# Revit family: FTXL Boiler.rfa
name_source: partatom
category: Mechanical Equipment
revit_build: Autodesk Revit MEP 2012 (Build: 20110916_2132(x64)
units: mm (PartAtom-declared; Revit-internal decimal feet)

## types (5) — shared parameters
# of Electrical Connections = 1
AIR INLET SIZE = 4"
Air Inlet Radius = 2"
Back Clearance = 24"
DEPTH = 22 1/2"
Description = FTXL Fire Tube Boiler
FUEL TYPE = NATURAL GAS
Front Clearance = 30"
Fuel Type = Natural or LP
GAS SIZE = 1"
Gas Radius = 1/2"
HEIGHT = 53 1/2"
Manufacturer = Lochinvar
Offset to Gas = 23 1/4"
SES BIM Studio # = 201464901-1
Top Clearance = 24"
URL = http://www.lochinvar.com
Voltage/Control = 24
Voltage/Heater = 120
WIDTH = 26 1/4"

## per-type parameters (varying)
| type | A_Total Depth | B_Depth to Flue Centerline | C_Flue Offset | D_Water Inlet Offset | E_Air Inlet Offset | F_Air Inlet Height | G_Gas Conn Height | H_Water Inlet Height | INPUT RATE (BTUH) | VENT SIZE | Vent Radius | WATER INLET SIZE | WATER OUTLET SIZE | Water Inlet Radius | Water Outlet Radius |
| FTX400 | 30 1/2" | 27 1/2" | 10 1/4" | 17" | 23 1/4" | 46 1/4" | 39 1/2" | 10 3/4" | 399.9 | 4" | 2" | 2" | 2" | 1" | 1" |
| FTX500 | 30 1/2" | 27 1/2" | 10 1/4" | 17" | 23 1/4" | 46 1/4" | 39 1/2" | 10 3/4" | 500 | 4" | 2" | 2" | 2" | 1" | 1" |
| FTX600 | 30 1/2" | 27 1/2" | 10 1/4" | 17" | 23 1/4" | 46 1/4" | 39 1/2" | 10 3/4" | 600 | 4" | 2" | 2" | 2" | 1" | 1" |
| FTX725 | 33" | 28 1/2" | 10 1/2" | 17 1/2" | 23 1/2" | 48 1/2" | 41 1/4" | 11" | 725 | 6" | 3" | 2 1/2" | 2 1/2" | 1 1/4" | 1 1/4" |
| FTX850 | 33" | 28 1/2" | 10 1/2" | 17 1/2" | 23 1/2" | 48 1/2" | 41 1/4" | 11" | 850 | 6" | 3" | 2 1/2" | 2 1/2" | 1 1/4" | 1 1/4" |

note: column(s) folded — value = type name in every type: MODEL NO., Model

## geometry (parser evidence)
native form markers: Sweep x1
no freeform markers — native parametric forms only
